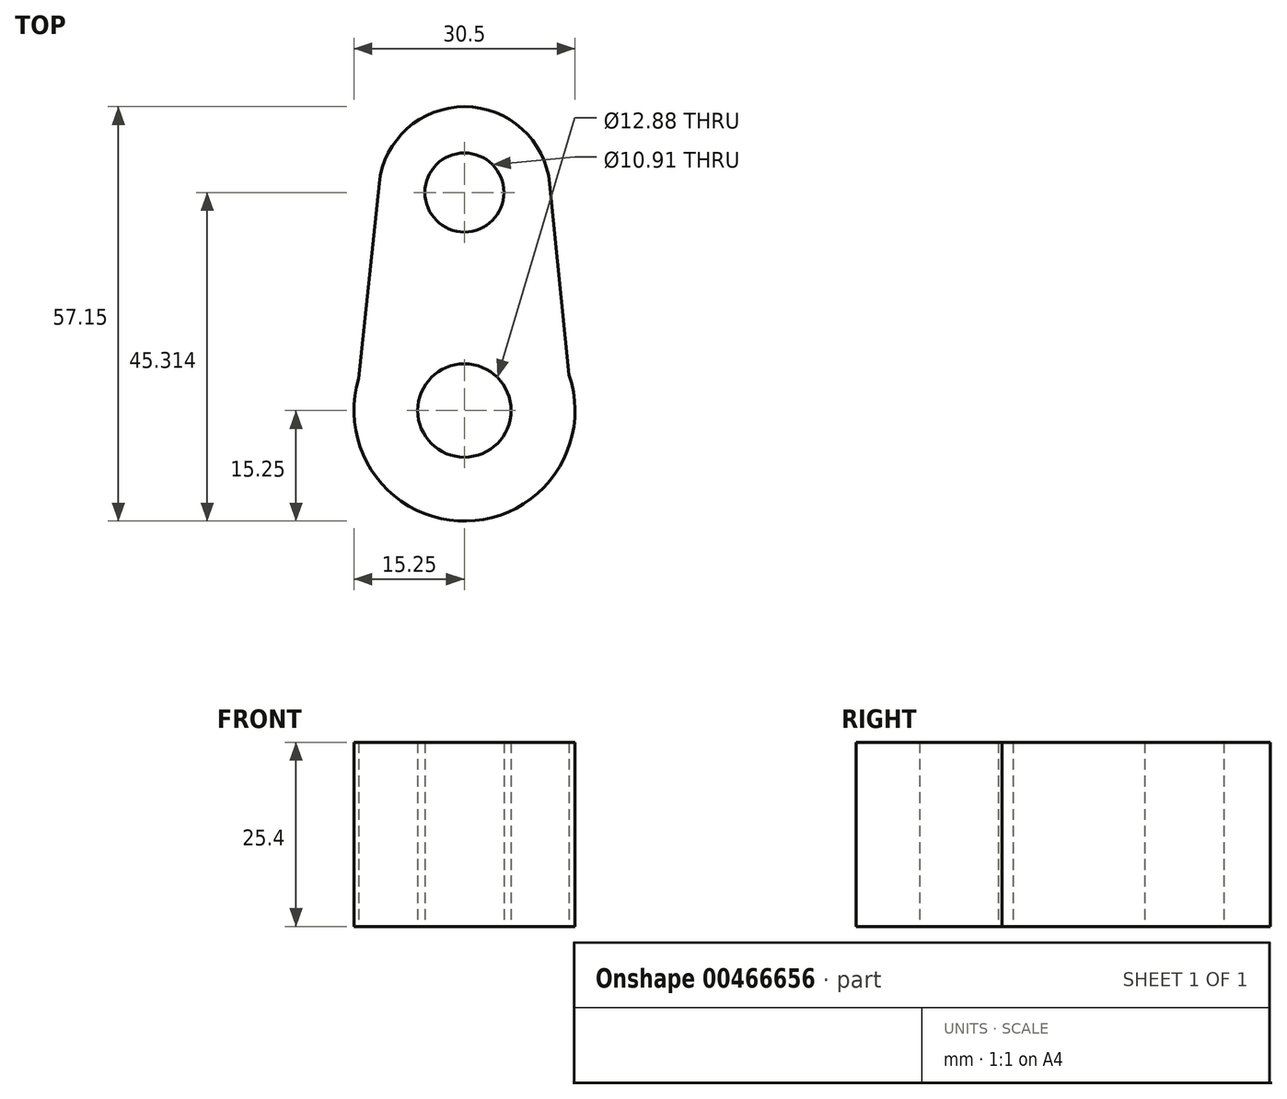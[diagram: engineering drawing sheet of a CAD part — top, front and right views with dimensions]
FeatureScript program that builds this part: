
annotation { "Feature Type Name" : "Feature", "Feature Type Description" : "" }
export const myFeature = defineFeature(function(context is Context, id is Id, definition is map)
    precondition{}
    {
        {
            var Q0;
            Q0=qCreatedBy(makeId("Top.planeOp"),FACE);
            var sketch = newSketch(context, id + "F0", { "sketchPlane" : qUnion([Q0])});
            skCircle(sketch, "E0", {"center": v(0, 0) * mm, "radius": 15.25 * mm});
            skCircle(sketch, "E1", {"center": v(0, 30.06) * mm, "radius": 11.83 * mm});
            skCircle(sketch, "E2", {"center": v(0, 30.06) * mm, "radius": 5.45 * mm});
            skCircle(sketch, "E3", {"center": v(0, 0) * mm, "radius": 6.44 * mm});
            skLineSegment(sketch, "E4", {"start": v(-11.77, 31.3) * mm, "end": v(-14.6, 4.4) * mm});
            skLineSegment(sketch, "E5", {"start": v(11.77, 31.26) * mm, "end": v(14.44, 4.92) * mm});
            skSolve(sketch);
        }
        {
            var Q0;
            Q0 = qSketchRegion(id + "F0", true);
            extrude(context, id + "F1", {"entities" : qUnion([Q0]), "endBound" : BoundingType.SYMMETRIC, "depth" : 25.4 * mm});
        }
    });
